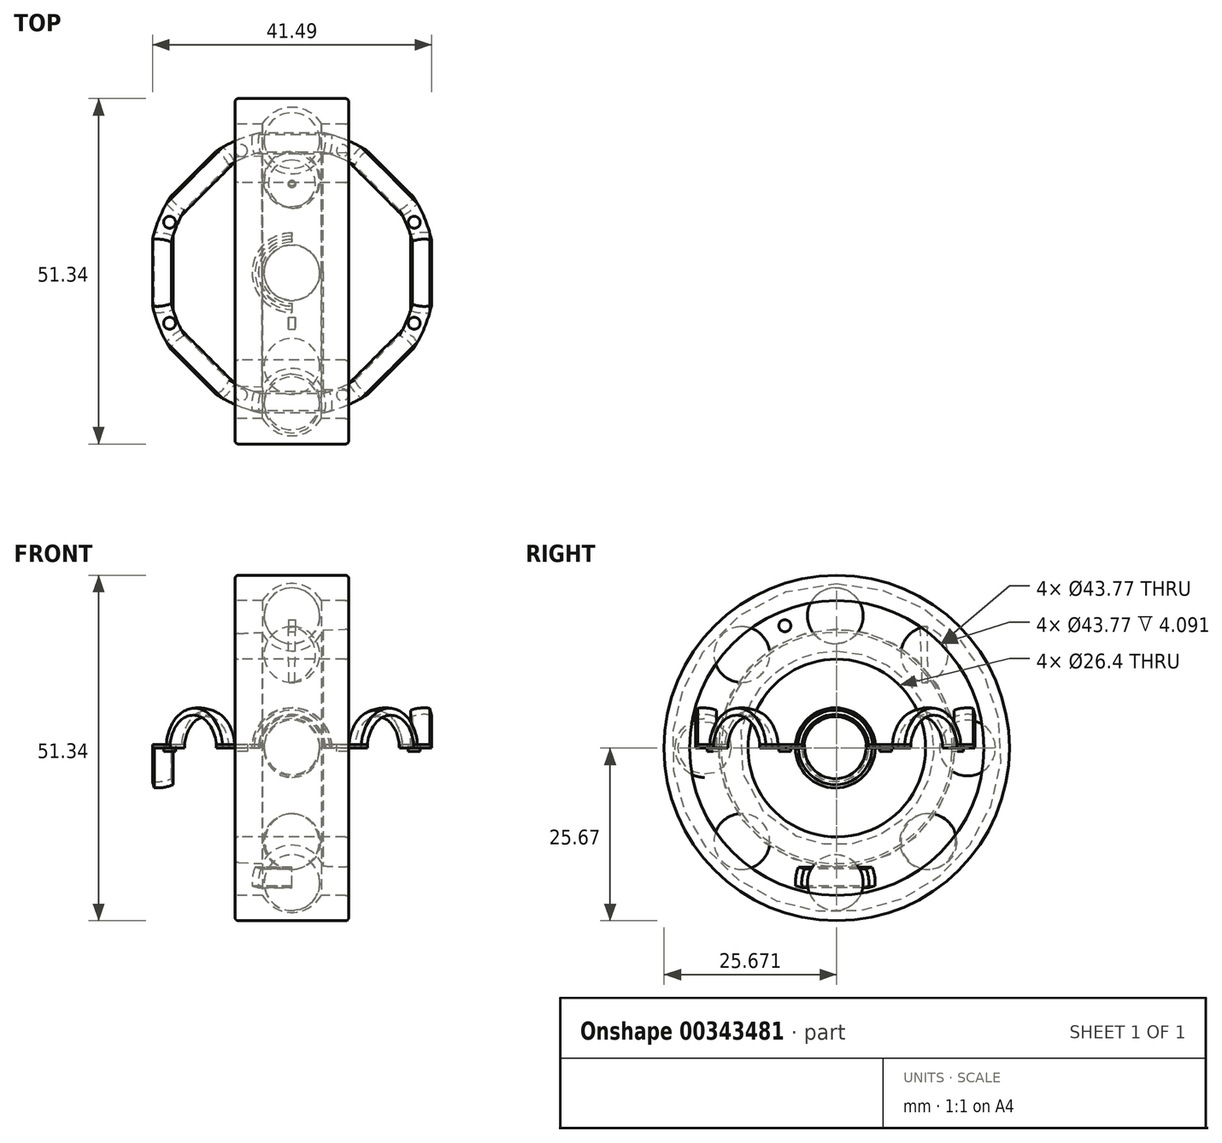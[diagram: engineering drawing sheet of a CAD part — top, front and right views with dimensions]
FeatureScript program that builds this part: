
annotation { "Feature Type Name" : "Feature", "Feature Type Description" : "" }
export const myFeature = defineFeature(function(context is Context, id is Id, definition is map)
    precondition{}
    {
        {
            assignVariable(context, id + "F0", {"name" : "t", "anyValue" : .5});
        }
        {
            var Q0;
            Q0=qCreatedBy(makeId("Top.planeOp"),FACE);
            var sketch = newSketch(context, id + "F1", { "sketchPlane" : qUnion([Q0])});
            skArc(sketch, "E0", {"start": v(-10.48, 32.8) * mm, "mid": v(-10.5, 31.35) * mm, "end": v(-10.18, 29.94) * mm});
            skArc(sketch, "E1", {"start": v(0.12, 30.21) * mm, "mid": v(-4.57, 36.97) * mm, "end": v(-9.25, 30.21) * mm});
            skCircle(sketch, "E2", {"center": v(-4.57, 31.97) * mm, "radius": 4.14 * mm});
            skCircle(sketch, "E3", {"center": v(-4.57, 12.32) * mm, "radius": 18.5 * mm});
            skCircle(sketch, "E4", {"center": v(-4.57, 12.32) * mm, "radius": 21.32 * mm});
            skArc(sketch, "E5", {"start": v(5.74, 30.98) * mm, "mid": v(4.7, 29.98) * mm, "end": v(3.93, 28.75) * mm});
            skArc(sketch, "E6", {"start": v(11.4, 21.66) * mm, "mid": v(12.86, 29.75) * mm, "end": v(4.78, 28.28) * mm});
            skCircle(sketch, "E7", {"center": v(9.33, 26.21) * mm, "radius": 4.14 * mm});
            skArc(sketch, "E8", {"start": v(15.91, 18.23) * mm, "mid": v(14.47, 18.26) * mm, "end": v(13.06, 17.93) * mm});
            skArc(sketch, "E9", {"start": v(13.33, 7.63) * mm, "mid": v(20.08, 12.32) * mm, "end": v(13.33, 17) * mm});
            skCircle(sketch, "E10", {"center": v(15.08, 12.32) * mm, "radius": 4.14 * mm});
            skArc(sketch, "E11", {"start": v(14.1, 2.02) * mm, "mid": v(13.1, 3.06) * mm, "end": v(11.87, 3.82) * mm});
            skArc(sketch, "E12", {"start": v(4.78, -3.65) * mm, "mid": v(12.86, -5.11) * mm, "end": v(11.4, 2.97) * mm});
            skCircle(sketch, "E13", {"center": v(9.33, -1.58) * mm, "radius": 4.14 * mm});
            skArc(sketch, "E14", {"start": v(1.35, -8.16) * mm, "mid": v(1.37, -6.72) * mm, "end": v(1.05, -5.31) * mm});
            skArc(sketch, "E15", {"start": v(-9.25, -5.58) * mm, "mid": v(-4.57, -12.33) * mm, "end": v(0.12, -5.58) * mm});
            skCircle(sketch, "E16", {"center": v(-4.57, -7.33) * mm, "radius": 4.14 * mm});
            skArc(sketch, "E17", {"start": v(-14.87, -6.35) * mm, "mid": v(-13.83, -5.34) * mm, "end": v(-13.06, -4.12) * mm});
            skArc(sketch, "E18", {"start": v(-20.53, 2.97) * mm, "mid": v(-22, -5.11) * mm, "end": v(-13.9, -3.65) * mm});
            skCircle(sketch, "E19", {"center": v(-18.46, -1.58) * mm, "radius": 4.14 * mm});
            skArc(sketch, "E20", {"start": v(-25.05, 6.4) * mm, "mid": v(-23.62, 6.47) * mm, "end": v(-22.25, 6.87) * mm});
            skArc(sketch, "E21", {"start": v(-22.5, 16.87) * mm, "mid": v(-29.57, 12.32) * mm, "end": v(-22.5, 7.77) * mm});
            skCircle(sketch, "E22", {"center": v(-24.57, 12.32) * mm, "radius": 4.14 * mm});
            skArc(sketch, "E23", {"start": v(-23.23, 22.62) * mm, "mid": v(-22.23, 21.58) * mm, "end": v(-21, 20.8) * mm});
            skArc(sketch, "E24", {"start": v(-13.9, 28.28) * mm, "mid": v(-22, 29.75) * mm, "end": v(-20.53, 21.66) * mm});
            skCircle(sketch, "E25", {"center": v(-18.46, 26.21) * mm, "radius": 4.14 * mm});
            skArc(sketch, "E26", {"start": v(-14.5, 29.26) * mm, "mid": v(-12.08, 30.46) * mm, "end": v(-9.52, 31.32) * mm});
            skArc(sketch, "E27", {"start": v(0.4, 31.32) * mm, "mid": v(2.95, 30.46) * mm, "end": v(5.37, 29.26) * mm});
            skArc(sketch, "E28", {"start": v(12.38, 22.25) * mm, "mid": v(13.58, 19.83) * mm, "end": v(14.44, 17.27) * mm});
            skArc(sketch, "E29", {"start": v(14.44, 7.36) * mm, "mid": v(13.58, 4.8) * mm, "end": v(12.38, 2.38) * mm});
            skArc(sketch, "E30", {"start": v(5.37, -4.63) * mm, "mid": v(2.95, -5.83) * mm, "end": v(0.4, -6.7) * mm});
            skArc(sketch, "E31", {"start": v(-9.52, -6.7) * mm, "mid": v(-12.08, -5.83) * mm, "end": v(-14.5, -4.63) * mm});
            skArc(sketch, "E32", {"start": v(-21.53, 2.37) * mm, "mid": v(-22.75, 4.82) * mm, "end": v(-23.61, 7.41) * mm});
            skArc(sketch, "E33", {"start": v(-23.6, 17.22) * mm, "mid": v(-22.74, 19.82) * mm, "end": v(-21.53, 22.26) * mm});
            skCircle(sketch, "E34", {"center": v(-12.08, 30.46) * mm, "radius": 0.89 * mm});
            skCircle(sketch, "E35", {"center": v(2.95, 30.46) * mm, "radius": 0.89 * mm});
            skCircle(sketch, "E36", {"center": v(13.58, 19.83) * mm, "radius": 0.89 * mm});
            skCircle(sketch, "E37", {"center": v(13.6, 4.82) * mm, "radius": 0.89 * mm});
            skCircle(sketch, "E38", {"center": v(13.62, 19.81) * mm, "radius": 0.89 * mm});
            skCircle(sketch, "E39", {"center": v(-22.74, 19.82) * mm, "radius": 0.89 * mm});
            skCircle(sketch, "E40", {"center": v(-22.75, 4.82) * mm, "radius": 0.89 * mm});
            skCircle(sketch, "E41", {"center": v(-12.08, -5.83) * mm, "radius": 0.89 * mm});
            skCircle(sketch, "E42", {"center": v(2.95, -5.83) * mm, "radius": 0.89 * mm});
            skSolve(sketch);
        }
        {
            var Q0;
            Q0=qCreatedBy(makeId("Top.planeOp"),FACE);
            var sketch = newSketch(context, id + "F2", { "sketchPlane" : qUnion([Q0])});
            skLineSegment(sketch, "E43.0", {"start": v(-14.32, 26.05) * mm, "end": v(-14.32, 26.05) * mm});
            skLineSegment(sketch, "E43.1", {"start": v(-20.43, 12.32) * mm, "end": v(-20.43, 12.32) * mm});
            skArc(sketch, "E43.2", {"start": v(-0.42, 31.97) * mm, "mid": v(-4.57, 36.1) * mm, "end": v(-8.7, 31.97) * mm});
            skLineSegment(sketch, "E43.3", {"start": v(5.19, 26.08) * mm, "end": v(5.19, 26.08) * mm});
            skLineSegment(sketch, "E43.4", {"start": v(10.94, 12.32) * mm, "end": v(10.94, 12.32) * mm});
            skLineSegment(sketch, "E43.5", {"start": v(5.19, -1.58) * mm, "end": v(5.19, -1.58) * mm});
            skArc(sketch, "E43.6", {"start": v(-0.43, -7.08) * mm, "mid": v(-4.6, -3.2) * mm, "end": v(-8.7, -7.14) * mm});
            skLineSegment(sketch, "E43.7", {"start": v(-14.32, -1.58) * mm, "end": v(-14.32, -1.58) * mm});
            skPoint(sketch, "E43.8", {"position": v(-4.57, 31.97) * mm});
            skPoint(sketch, "E43.9", {"position": v(-18.46, 26.21) * mm});
            skPoint(sketch, "E43.10", {"position": v(-24.57, 12.32) * mm});
            skPoint(sketch, "E43.11", {"position": v(-18.46, -1.58) * mm});
            skPoint(sketch, "E43.12", {"position": v(-4.57, -7.33) * mm});
            skPoint(sketch, "E43.13", {"position": v(9.33, -1.58) * mm});
            skPoint(sketch, "E43.14", {"position": v(15.08, 12.32) * mm});
            skPoint(sketch, "E43.15", {"position": v(9.33, 26.21) * mm});
            skLineSegment(sketch, "E44", {"start": v(-42.22, 31.97) * mm, "end": v(40.03, 31.97) * mm});
            skArc(sketch, "E45.0", {"start": v(-14.32, 26.05) * mm, "mid": v(-18.38, 30.35) * mm, "end": v(-22.6, 26.21) * mm});
            skArc(sketch, "E45.1", {"start": v(13.47, 26.03) * mm, "mid": v(9.36, 30.35) * mm, "end": v(5.19, 26.08) * mm});
            skArc(sketch, "E45.2", {"start": v(19.23, 12.32) * mm, "mid": v(15.08, 16.46) * mm, "end": v(10.94, 12.32) * mm});
            skArc(sketch, "E45.3", {"start": v(13.47, -1.58) * mm, "mid": v(9.33, 2.56) * mm, "end": v(5.19, -1.58) * mm});
            skArc(sketch, "E45.4", {"start": v(-14.32, -1.58) * mm, "mid": v(-18.46, 2.56) * mm, "end": v(-22.6, -1.58) * mm});
            skArc(sketch, "E45.5", {"start": v(-20.43, 12.32) * mm, "mid": v(-24.57, 16.46) * mm, "end": v(-28.72, 12.32) * mm});
            skLineSegment(sketch, "E46", {"start": v(-22.6, 26.21) * mm, "end": v(-14.32, 26.05) * mm});
            skLineSegment(sketch, "E47", {"start": v(5.19, 26.08) * mm, "end": v(13.47, 26.03) * mm});
            skLineSegment(sketch, "E48", {"start": v(-28.72, 12.32) * mm, "end": v(19.23, 12.32) * mm});
            skLineSegment(sketch, "E49", {"start": v(-8.7, -7.14) * mm, "end": v(-0.43, -7.08) * mm});
            skLineSegment(sketch, "E50", {"start": v(-18.46, -1.58) * mm, "end": v(9.33, -1.58) * mm});
            skLineSegment(sketch, "E51", {"start": v(9.33, -1.58) * mm, "end": v(16.13, -1.58) * mm});
            skLineSegment(sketch, "E52", {"start": v(-18.46, -1.58) * mm, "end": v(-25.22, -1.58) * mm});
            skSolve(sketch);
        }
        {
            var Q0;
            {var subQ0=sQuery(id+"F2.wireOp",EDGE,"E46");Q0=makeQuery(id+"F2.imprint","IMPRINT",FACE,{"disambiguationData":[TD([[makeQuery(id+"F2.imprint","IMPRINT",EDGE,{"derivedFrom":subQ0}),1.0]])]});}
            var Q1;
            {var subQ0=sQuery(id+"F2.wireOp",EDGE,"E47");Q1=makeQuery(id+"F2.imprint","IMPRINT",FACE,{"disambiguationData":[TD([[makeQuery(id+"F2.imprint","IMPRINT",EDGE,{"derivedFrom":subQ0}),1.0]])]});}
            var Q2;
            Q2=sQuery(id+"F2.wireOp",EDGE,"E46");
            revolve(context, id + "F3", {"entities" : qUnion([Q0, Q1]), "axis" : qUnion([Q2]), "revolveType" : RevolveType.FULL});
        }
        {
            var Q0;
            {var subQ0=sQuery(id+"F2.wireOp",EDGE,"E43.2");Q0=makeQuery(id+"F2.imprint","IMPRINT",FACE,{"disambiguationData":[TD([[makeQuery(id+"F2.imprint","IMPRINT",EDGE,{"derivedFrom":subQ0}),1.0]])]});}
            var Q1;
            Q1=sQuery(id+"F2.wireOp",EDGE,"E44");
            revolve(context, id + "F4", {"entities" : qUnion([Q0]), "axis" : qUnion([Q1]), "revolveType" : RevolveType.FULL});
        }
        {
            var Q0;
            {var subQ0=sQuery(id+"F2.wireOp",EDGE,"E45.5");Q0=makeQuery(id+"F2.imprint","IMPRINT",FACE,{"disambiguationData":[TD([[makeQuery(id+"F2.imprint","IMPRINT",EDGE,{"derivedFrom":subQ0}),1.0]])]});}
            var Q1;
            {var subQ0=sQuery(id+"F2.wireOp",EDGE,"E45.2");Q1=makeQuery(id+"F2.imprint","IMPRINT",FACE,{"disambiguationData":[TD([[makeQuery(id+"F2.imprint","IMPRINT",EDGE,{"derivedFrom":subQ0}),1.0]])]});}
            var Q2;
            Q2=sQuery(id+"F2.wireOp",EDGE,"E48");
            revolve(context, id + "F5", {"entities" : qUnion([Q0, Q1]), "axis" : qUnion([Q2]), "revolveType" : RevolveType.FULL});
        }
        {
            var Q0;
            {var subQ0=sQuery(id+"F2.wireOp",EDGE,"E45.3");Q0=makeQuery(id+"F2.imprint","IMPRINT",FACE,{"disambiguationData":[TD([[makeQuery(id+"F2.imprint","IMPRINT",EDGE,{"derivedFrom":subQ0}),1.0]])]});}
            var Q1;
            {var subQ0=sQuery(id+"F2.wireOp",EDGE,"E45.4");Q1=makeQuery(id+"F2.imprint","IMPRINT",FACE,{"disambiguationData":[TD([[makeQuery(id+"F2.imprint","IMPRINT",EDGE,{"derivedFrom":subQ0}),1.0]])]});}
            var Q2;
            Q2=sQuery(id+"F2.wireOp",EDGE,"E50");
            revolve(context, id + "F6", {"entities" : qUnion([Q0, Q1]), "axis" : qUnion([Q2]), "revolveType" : RevolveType.FULL});
        }
        {
            var Q0;
            Q0=makeQuery(id+"F2.imprint","IMPRINT",FACE,{"disambiguationData":[TD([[makeQuery(id+"F2.imprint","IMPRINT",EDGE,{"derivedFrom":sQuery(id+"F2.wireOp",EDGE,"E43.6")}),1.0]])]});
            var Q1;
            Q1=sQuery(id+"F2.wireOp",EDGE,"E49");
            revolve(context, id + "F7", {"entities" : qUnion([Q0]), "axis" : qUnion([Q1]), "revolveType" : RevolveType.FULL});
        }
        {
            var Q0;
            Q0=qCreatedBy(makeId("Top.planeOp"),FACE);
            var sketch = newSketch(context, id + "F8", { "sketchPlane" : qUnion([Q0])});
            skArc(sketch, "E53.0", {"start": v(-23.23, 22.62) * mm, "mid": v(-22.23, 21.58) * mm, "end": v(-21, 20.8) * mm});
            skArc(sketch, "E53.1", {"start": v(-25.05, 6.4) * mm, "mid": v(-23.62, 6.47) * mm, "end": v(-22.25, 6.87) * mm});
            skArc(sketch, "E53.2", {"start": v(-10.48, 32.8) * mm, "mid": v(-10.5, 31.35) * mm, "end": v(-10.18, 29.94) * mm});
            skArc(sketch, "E53.3", {"start": v(5.74, 30.98) * mm, "mid": v(4.7, 29.98) * mm, "end": v(3.93, 28.75) * mm});
            skArc(sketch, "E53.4", {"start": v(15.91, 18.23) * mm, "mid": v(14.47, 18.26) * mm, "end": v(13.06, 17.93) * mm});
            skArc(sketch, "E53.5", {"start": v(14.1, 2.02) * mm, "mid": v(13.1, 3.06) * mm, "end": v(11.87, 3.82) * mm});
            skArc(sketch, "E53.6", {"start": v(1.35, -8.16) * mm, "mid": v(1.37, -6.72) * mm, "end": v(1.05, -5.31) * mm});
            skArc(sketch, "E53.7", {"start": v(-14.87, -6.35) * mm, "mid": v(-13.83, -5.34) * mm, "end": v(-13.06, -4.12) * mm});
            skPoint(sketch, "E53.8", {"position": v(-4.57, 31.97) * mm});
            skPoint(sketch, "E53.9", {"position": v(9.33, 26.21) * mm});
            skPoint(sketch, "E53.10", {"position": v(15.08, 12.32) * mm});
            skPoint(sketch, "E53.11", {"position": v(9.33, -1.58) * mm});
            skPoint(sketch, "E53.12", {"position": v(-4.57, -7.33) * mm});
            skPoint(sketch, "E53.13", {"position": v(-18.46, -1.58) * mm});
            skPoint(sketch, "E53.14", {"position": v(-24.57, 12.32) * mm});
            skPoint(sketch, "E53.15", {"position": v(-18.46, 26.21) * mm});
            skArc(sketch, "E53.16", {"start": v(0.12, 30.21) * mm, "mid": v(0.42, 31.63) * mm, "end": v(0.31, 33.07) * mm});
            skArc(sketch, "E53.17", {"start": v(11.4, 21.66) * mm, "mid": v(12.62, 22.44) * mm, "end": v(13.56, 23.54) * mm});
            skArc(sketch, "E53.18", {"start": v(13.33, 7.63) * mm, "mid": v(14.74, 7.33) * mm, "end": v(16.19, 7.44) * mm});
            skArc(sketch, "E53.19", {"start": v(4.78, -3.65) * mm, "mid": v(5.56, -4.87) * mm, "end": v(6.66, -5.8) * mm});
            skArc(sketch, "E53.20", {"start": v(-9.25, -5.58) * mm, "mid": v(-9.55, -7) * mm, "end": v(-9.44, -8.44) * mm});
            skArc(sketch, "E53.21", {"start": v(-20.53, 2.97) * mm, "mid": v(-21.75, 2.19) * mm, "end": v(-22.69, 1.1) * mm});
            skArc(sketch, "E53.22", {"start": v(-22.5, 16.87) * mm, "mid": v(-23.87, 17.27) * mm, "end": v(-25.3, 17.27) * mm});
            skArc(sketch, "E53.23", {"start": v(-13.9, 28.28) * mm, "mid": v(-14.7, 29.5) * mm, "end": v(-15.8, 30.44) * mm});
            skCircle(sketch, "E54.0", {"center": v(-4.57, 12.32) * mm, "radius": 21.32 * mm});
            skCircle(sketch, "E55.0", {"center": v(-4.57, 12.32) * mm, "radius": 18.5 * mm});
            skArc(sketch, "E56.trimOffspring", {"start": v(-22.69, 23.54) * mm, "mid": v(-21.75, 22.44) * mm, "end": v(-20.53, 21.66) * mm});
            skArc(sketch, "E57.trimOffspring", {"start": v(-9.44, 33.07) * mm, "mid": v(-9.55, 31.63) * mm, "end": v(-9.25, 30.21) * mm});
            skArc(sketch, "E58.trimOffspring", {"start": v(6.66, 30.44) * mm, "mid": v(5.56, 29.5) * mm, "end": v(4.78, 28.28) * mm});
            skArc(sketch, "E59.trimOffspring", {"start": v(16.19, 17.2) * mm, "mid": v(14.74, 17.3) * mm, "end": v(13.33, 17) * mm});
            skArc(sketch, "E60.trimOffspring", {"start": v(13.56, 1.1) * mm, "mid": v(12.62, 2.19) * mm, "end": v(11.4, 2.97) * mm});
            skArc(sketch, "E61.trimOffspring", {"start": v(0.31, -8.44) * mm, "mid": v(0.42, -7) * mm, "end": v(0.12, -5.58) * mm});
            skArc(sketch, "E62.trimOffspring", {"start": v(-15.8, -5.8) * mm, "mid": v(-14.7, -4.87) * mm, "end": v(-13.9, -3.65) * mm});
            skArc(sketch, "E63.trimOffspring", {"start": v(-25.3, 7.37) * mm, "mid": v(-23.87, 7.37) * mm, "end": v(-22.5, 7.77) * mm});
            skLineSegment(sketch, "E64", {"start": v(-18.46, -1.58) * mm, "end": v(9.33, 26.21) * mm, "construction": true});
            skLineSegment(sketch, "E65", {"start": v(-18.46, 26.21) * mm, "end": v(9.33, -1.58) * mm, "construction": true});
            skLineSegment(sketch, "E66", {"start": v(-24.57, 12.32) * mm, "end": v(15.08, 12.32) * mm, "construction": true});
            skLineSegment(sketch, "E67", {"start": v(-4.57, 31.97) * mm, "end": v(-4.57, -7.33) * mm, "construction": true});
            skSolve(sketch);
        }
        {
            var Q0;
            {var subQ0=sQuery(id+"F8.wireOp",EDGE,"E53.0");Q0=makeQuery(id+"F8.imprint","IMPRINT",FACE,{"disambiguationData":[TD([[makeQuery(id+"F8.imprint","IMPRINT",EDGE,{"derivedFrom":subQ0}),1.0]])]});}
            var Q1;
            Q1=sQuery(id+"F8.wireOp",EDGE,"E65");
            revolve(context, id + "F9", {"entities" : qUnion([Q0]), "axis" : qUnion([Q1]), "revolveType" : RevolveType.ONE_DIRECTION, "oppositeDirection" : true, "angle" : 180 * degree});
        }
        {
            var Q0;
            {var subQ0=sQuery(id+"F8.wireOp",EDGE,"E53.2");Q0=makeQuery(id+"F8.imprint","IMPRINT",FACE,{"disambiguationData":[TD([[makeQuery(id+"F8.imprint","IMPRINT",EDGE,{"derivedFrom":subQ0}),1.0]])]});}
            var Q1;
            Q1=sQuery(id+"F8.wireOp",EDGE,"E67");
            revolve(context, id + "F10", {"entities" : qUnion([Q0]), "axis" : qUnion([Q1]), "revolveType" : RevolveType.ONE_DIRECTION, "oppositeDirection" : true, "angle" : 180 * degree});
        }
        {
            var Q0;
            {var subQ0=sQuery(id+"F8.wireOp",EDGE,"E53.3");Q0=makeQuery(id+"F8.imprint","IMPRINT",FACE,{"disambiguationData":[TD([[makeQuery(id+"F8.imprint","IMPRINT",EDGE,{"derivedFrom":subQ0}),1.0]])]});}
            var Q1;
            Q1=sQuery(id+"F8.wireOp",EDGE,"E64");
            revolve(context, id + "F11", {"entities" : qUnion([Q0]), "axis" : qUnion([Q1]), "revolveType" : RevolveType.ONE_DIRECTION, "angle" : 180 * degree});
        }
        {
            var Q0;
            {var subQ0=sQuery(id+"F8.wireOp",EDGE,"E53.4");Q0=makeQuery(id+"F8.imprint","IMPRINT",FACE,{"disambiguationData":[TD([[makeQuery(id+"F8.imprint","IMPRINT",EDGE,{"derivedFrom":subQ0}),1.0]])]});}
            var Q1;
            Q1=sQuery(id+"F8.wireOp",EDGE,"E66");
            revolve(context, id + "F12", {"entities" : qUnion([Q0]), "axis" : qUnion([Q1]), "revolveType" : RevolveType.ONE_DIRECTION, "angle" : 180 * degree});
        }
        {
            var Q0;
            {var subQ0=sQuery(id+"F8.wireOp",EDGE,"E53.5");Q0=makeQuery(id+"F8.imprint","IMPRINT",FACE,{"disambiguationData":[TD([[makeQuery(id+"F8.imprint","IMPRINT",EDGE,{"derivedFrom":subQ0}),1.0]])]});}
            var Q1;
            Q1=sQuery(id+"F8.wireOp",EDGE,"E65");
            revolve(context, id + "F13", {"entities" : qUnion([Q0]), "axis" : qUnion([Q1]), "revolveType" : RevolveType.ONE_DIRECTION, "angle" : 180 * degree});
        }
        {
            var Q0;
            {var subQ0=sQuery(id+"F8.wireOp",EDGE,"E53.6");Q0=makeQuery(id+"F8.imprint","IMPRINT",FACE,{"disambiguationData":[TD([[makeQuery(id+"F8.imprint","IMPRINT",EDGE,{"derivedFrom":subQ0}),1.0]])]});}
            var Q1;
            Q1=sQuery(id+"F8.wireOp",EDGE,"E67");
            revolve(context, id + "F14", {"entities" : qUnion([Q0]), "axis" : qUnion([Q1]), "revolveType" : RevolveType.ONE_DIRECTION, "angle" : 180 * degree});
        }
        {
            var Q0;
            {var subQ0=sQuery(id+"F8.wireOp",EDGE,"E53.7");Q0=makeQuery(id+"F8.imprint","IMPRINT",FACE,{"disambiguationData":[TD([[makeQuery(id+"F8.imprint","IMPRINT",EDGE,{"derivedFrom":subQ0}),1.0]])]});}
            var Q1;
            Q1=sQuery(id+"F8.wireOp",EDGE,"E64");
            revolve(context, id + "F15", {"entities" : qUnion([Q0]), "axis" : qUnion([Q1]), "revolveType" : RevolveType.ONE_DIRECTION, "oppositeDirection" : true, "angle" : 180 * degree});
        }
        {
            var Q0;
            {var subQ0=sQuery(id+"F8.wireOp",EDGE,"E53.1");Q0=makeQuery(id+"F8.imprint","IMPRINT",FACE,{"disambiguationData":[TD([[makeQuery(id+"F8.imprint","IMPRINT",EDGE,{"derivedFrom":subQ0}),1.0]])]});}
            var Q1;
            Q1=sQuery(id+"F8.wireOp",EDGE,"E66");
            revolve(context, id + "F16", {"entities" : qUnion([Q0]), "axis" : qUnion([Q1]), "revolveType" : RevolveType.ONE_DIRECTION, "oppositeDirection" : true, "angle" : 180 * degree});
        }
        {
            var Q0;
            Q0=qCreatedBy(makeId("Top.planeOp"),FACE);
            var sketch = newSketch(context, id + "F17", { "sketchPlane" : qUnion([Q0])});
            skArc(sketch, "E68.0", {"start": v(-13.9, 28.28) * mm, "mid": v(-14.7, 29.5) * mm, "end": v(-15.8, 30.44) * mm});
            skArc(sketch, "E68.1", {"start": v(-9.44, 33.07) * mm, "mid": v(-9.55, 31.63) * mm, "end": v(-9.25, 30.21) * mm});
            skArc(sketch, "E68.2", {"start": v(0.12, 30.21) * mm, "mid": v(0.42, 31.63) * mm, "end": v(0.31, 33.07) * mm});
            skArc(sketch, "E68.3", {"start": v(6.66, 30.44) * mm, "mid": v(5.56, 29.5) * mm, "end": v(4.78, 28.28) * mm});
            skArc(sketch, "E68.4", {"start": v(11.4, 21.66) * mm, "mid": v(12.62, 22.44) * mm, "end": v(13.56, 23.54) * mm});
            skArc(sketch, "E68.5", {"start": v(16.19, 17.2) * mm, "mid": v(14.74, 17.3) * mm, "end": v(13.33, 17) * mm});
            skArc(sketch, "E68.6", {"start": v(13.33, 7.63) * mm, "mid": v(14.74, 7.33) * mm, "end": v(16.19, 7.44) * mm});
            skArc(sketch, "E68.7", {"start": v(13.56, 1.1) * mm, "mid": v(12.62, 2.19) * mm, "end": v(11.4, 2.97) * mm});
            skArc(sketch, "E68.8", {"start": v(4.78, -3.65) * mm, "mid": v(5.56, -4.87) * mm, "end": v(6.66, -5.8) * mm});
            skArc(sketch, "E68.10", {"start": v(-9.25, -5.58) * mm, "mid": v(-9.55, -7) * mm, "end": v(-9.44, -8.44) * mm});
            skArc(sketch, "E68.11", {"start": v(-15.8, -5.8) * mm, "mid": v(-14.7, -4.87) * mm, "end": v(-13.9, -3.65) * mm});
            skArc(sketch, "E68.12", {"start": v(-20.53, 2.97) * mm, "mid": v(-21.75, 2.19) * mm, "end": v(-22.69, 1.1) * mm});
            skArc(sketch, "E68.13", {"start": v(-25.3, 7.37) * mm, "mid": v(-23.87, 7.37) * mm, "end": v(-22.5, 7.77) * mm});
            skArc(sketch, "E68.14", {"start": v(-22.5, 16.87) * mm, "mid": v(-23.87, 17.27) * mm, "end": v(-25.3, 17.27) * mm});
            skArc(sketch, "E68.15", {"start": v(-22.69, 23.54) * mm, "mid": v(-21.75, 22.44) * mm, "end": v(-20.53, 21.66) * mm});
            skCircle(sketch, "E68.16", {"center": v(-4.57, 12.32) * mm, "radius": 18.5 * mm});
            skCircle(sketch, "E68.17", {"center": v(-4.57, 12.32) * mm, "radius": 21.32 * mm});
            skCircle(sketch, "E69.0", {"center": v(-12.08, 30.46) * mm, "radius": 0.89 * mm});
            skCircle(sketch, "E69.1", {"center": v(-22.74, 19.82) * mm, "radius": 0.89 * mm});
            skCircle(sketch, "E69.2", {"center": v(2.95, 30.46) * mm, "radius": 0.89 * mm});
            skCircle(sketch, "E69.3", {"center": v(13.62, 19.81) * mm, "radius": 0.89 * mm});
            skCircle(sketch, "E69.4", {"center": v(13.6, 4.82) * mm, "radius": 0.89 * mm});
            skCircle(sketch, "E69.5", {"center": v(2.95, -5.83) * mm, "radius": 0.89 * mm});
            skCircle(sketch, "E69.6", {"center": v(-12.08, -5.83) * mm, "radius": 0.89 * mm});
            skCircle(sketch, "E69.7", {"center": v(-22.75, 4.82) * mm, "radius": 0.89 * mm});
            skArc(sketch, "E70.0", {"start": v(0.31, -8.44) * mm, "mid": v(0.42, -7) * mm, "end": v(0.12, -5.58) * mm});
            skSolve(sketch);
        }
        {
            var Q0;
            {var subQ1=sQuery(id+"F17.wireOp",EDGE,"E68.6");Q0=makeQuery(id+"F17.imprint","IMPRINT",FACE,{"disambiguationData":[TD([[makeQuery(id+"F17.imprint","IMPRINT",EDGE,{"derivedFrom":subQ1}),-1.0]])]});}
            var Q1;
            {var subQ1=sQuery(id+"F17.wireOp",EDGE,"E68.8");Q1=makeQuery(id+"F17.imprint","IMPRINT",FACE,{"disambiguationData":[TD([[makeQuery(id+"F17.imprint","IMPRINT",EDGE,{"derivedFrom":subQ1}),-1.0]])]});}
            var Q2;
            {var subQ1=sQuery(id+"F17.wireOp",EDGE,"E68.10");Q2=makeQuery(id+"F17.imprint","IMPRINT",FACE,{"disambiguationData":[TD([[makeQuery(id+"F17.imprint","IMPRINT",EDGE,{"derivedFrom":subQ1}),-1.0]])]});}
            var Q3;
            {var subQ1=sQuery(id+"F17.wireOp",EDGE,"E68.12");Q3=makeQuery(id+"F17.imprint","IMPRINT",FACE,{"disambiguationData":[TD([[makeQuery(id+"F17.imprint","IMPRINT",EDGE,{"derivedFrom":subQ1}),-1.0]])]});}
            var Q4;
            {var subQ1=sQuery(id+"F17.wireOp",EDGE,"E68.14");Q4=makeQuery(id+"F17.imprint","IMPRINT",FACE,{"disambiguationData":[TD([[makeQuery(id+"F17.imprint","IMPRINT",EDGE,{"derivedFrom":subQ1}),-1.0]])]});}
            var Q5;
            {var subQ1=sQuery(id+"F17.wireOp",EDGE,"E68.0");Q5=makeQuery(id+"F17.imprint","IMPRINT",FACE,{"disambiguationData":[TD([[makeQuery(id+"F17.imprint","IMPRINT",EDGE,{"derivedFrom":subQ1}),-1.0]])]});}
            var Q6;
            {var subQ1=sQuery(id+"F17.wireOp",EDGE,"E68.2");Q6=makeQuery(id+"F17.imprint","IMPRINT",FACE,{"disambiguationData":[TD([[makeQuery(id+"F17.imprint","IMPRINT",EDGE,{"derivedFrom":subQ1}),-1.0]])]});}
            var Q7;
            {var subQ1=sQuery(id+"F17.wireOp",EDGE,"E68.4");Q7=makeQuery(id+"F17.imprint","IMPRINT",FACE,{"disambiguationData":[TD([[makeQuery(id+"F17.imprint","IMPRINT",EDGE,{"derivedFrom":subQ1}),-1.0]])]});}
            extrude(context, id + "F18", {"entities" : qUnion([Q0, Q1, Q2, Q3, Q4, Q5, Q6, Q7]), "depth" : (getVariable(context, 't')) * mm});
        }
        {
            var Q0;
            Q0=makeQuery(id+"F16.opRevolve","SWEPT_BODY",BODY,{"disambiguationData":[OSD([sQuery(id+"F8.wireOp",EDGE,"E53.1"),sQuery(id+"F8.wireOp",EDGE,"E54.0"),sQuery(id+"F8.wireOp",EDGE,"E55.0"),sQuery(id+"F8.wireOp",EDGE,"E63.trimOffspring")])]});
            transform(context, id + "F19", {"entities" : qUnion([Q0]), "transformType" : TransformType.COPY});
        }
        {
            var Q0;
            Q0=makeQuery(id+"F19.opPattern","COPY",BODY,{"derivedFrom":makeQuery(id+"F16.opRevolve","SWEPT_BODY",BODY,{"disambiguationData":[OSD([sQuery(id+"F8.wireOp",EDGE,"E53.1"),sQuery(id+"F8.wireOp",EDGE,"E54.0"),sQuery(id+"F8.wireOp",EDGE,"E55.0"),sQuery(id+"F8.wireOp",EDGE,"E63.trimOffspring")])]}),"instanceName":"1"});
            var Q1;
            Q1=sQuery(id+"F2.wireOp",EDGE,"E48");
            transform(context, id + "F20", {"entities" : qUnion([Q0]), "transformType" : TransformType.ROTATION, "transformAxis" : qUnion([Q1]), "angle" : 180 * degree, "makeCopy" : false});
        }
        {
            var Q0;
            Q0=makeQuery(id+"F17.imprint","IMPRINT",FACE,{"disambiguationData":[TD([[makeQuery(id+"F17.imprint","IMPRINT",EDGE,{"derivedFrom":sQuery(id+"F17.wireOp",EDGE,"E69.6")}),1.0]])]});
            var Q1;
            Q1=makeQuery(id+"F17.imprint","IMPRINT",FACE,{"disambiguationData":[TD([[makeQuery(id+"F17.imprint","IMPRINT",EDGE,{"derivedFrom":sQuery(id+"F17.wireOp",EDGE,"E69.7")}),1.0]])]});
            var Q2;
            Q2=makeQuery(id+"F17.imprint","IMPRINT",FACE,{"disambiguationData":[TD([[makeQuery(id+"F17.imprint","IMPRINT",EDGE,{"derivedFrom":sQuery(id+"F17.wireOp",EDGE,"E69.1")}),1.0]])]});
            var Q3;
            Q3=makeQuery(id+"F17.imprint","IMPRINT",FACE,{"disambiguationData":[TD([[makeQuery(id+"F17.imprint","IMPRINT",EDGE,{"derivedFrom":sQuery(id+"F17.wireOp",EDGE,"E69.0")}),1.0]])]});
            var Q4;
            Q4=makeQuery(id+"F17.imprint","IMPRINT",FACE,{"disambiguationData":[TD([[makeQuery(id+"F17.imprint","IMPRINT",EDGE,{"derivedFrom":sQuery(id+"F17.wireOp",EDGE,"E69.2")}),1.0]])]});
            var Q5;
            Q5=makeQuery(id+"F17.imprint","IMPRINT",FACE,{"disambiguationData":[TD([[makeQuery(id+"F17.imprint","IMPRINT",EDGE,{"derivedFrom":sQuery(id+"F17.wireOp",EDGE,"E69.3")}),1.0]])]});
            var Q6;
            Q6=makeQuery(id+"F17.imprint","IMPRINT",FACE,{"disambiguationData":[TD([[makeQuery(id+"F17.imprint","IMPRINT",EDGE,{"derivedFrom":sQuery(id+"F17.wireOp",EDGE,"E69.4")}),1.0]])]});
            var Q7;
            Q7=makeQuery(id+"F17.imprint","IMPRINT",FACE,{"disambiguationData":[TD([[makeQuery(id+"F17.imprint","IMPRINT",EDGE,{"derivedFrom":sQuery(id+"F17.wireOp",EDGE,"E69.5")}),1.0]])]});
            extrude(context, id + "F21", {"entities" : qUnion([Q0, Q1, Q2, Q3, Q4, Q5, Q6, Q7]), "endBound" : BoundingType.SYMMETRIC, "depth" : 1 * mm});
        }
        {
            var Q0;
            {var subQ0=sQuery(id+"F1.wireOp",EDGE,"E4");var subQ1=sQuery(id+"F1.wireOp",EDGE,"E2");var subQ2=makeQuery(id+"F1.imprint","INTERSECT",VERTEX,{"disambiguationData":[OD(0.0)],"derivedFrom":[subQ1,subQ0]});Q0=makeQuery(id+"F1.imprint","IMPRINT",FACE,{"disambiguationData":[TD([[makeQuery(id+"F1.imprint","IMPRINT",EDGE,{"disambiguationData":[TD([[subQ2,1.0]])],"derivedFrom":subQ1}),1.0]])]});}
            var sketch = newSketch(context, id + "F22", { "sketchPlane" : qUnion([Q0])});
            skCircle(sketch, "E71.0", {"center": v(-4.57, 31.97) * mm, "radius": 4.14 * mm});
            skArc(sketch, "E72.0", {"start": v(0.12, 30.21) * mm, "mid": v(-4.57, 36.97) * mm, "end": v(-9.25, 30.21) * mm});
            skArc(sketch, "E73.0.1", {"start": v(-0.63, 33.27) * mm, "mid": v(-4.57, 36.1) * mm, "end": v(-8.5, 33.27) * mm});
            skArc(sketch, "E73.1.0", {"start": v(-8.4, 30.41) * mm, "mid": v(-4.57, 27.82) * mm, "end": v(-0.72, 30.41) * mm});
            skArc(sketch, "E73.3.1", {"start": v(-0.72, 30.41) * mm, "mid": v(-0.42, 31.83) * mm, "end": v(-0.63, 33.27) * mm});
            skArc(sketch, "E73.3.3", {"start": v(-8.5, 33.27) * mm, "mid": v(-8.7, 31.83) * mm, "end": v(-8.4, 30.41) * mm});
            skCircle(sketch, "E74", {"center": v(-4.57, 31.97) * mm, "radius": 5 * mm});
            skLineSegment(sketch, "E75.bottom", {"start": v(3.88, 25.73) * mm, "end": v(-13.01, 25.73) * mm});
            skLineSegment(sketch, "E75.top", {"start": v(3.88, 38.2) * mm, "end": v(-13.01, 38.2) * mm});
            skLineSegment(sketch, "E75.left", {"start": v(3.88, 25.73) * mm, "end": v(3.88, 38.2) * mm});
            skLineSegment(sketch, "E75.right", {"start": v(-13.01, 25.73) * mm, "end": v(-13.01, 38.2) * mm});
            skArc(sketch, "E76.trimOffspring", {"start": v(-13.01, 28.32) * mm, "mid": v(-4.57, -5.38) * mm, "end": v(3.88, 28.32) * mm});
            skArc(sketch, "E77.trimOffspring", {"start": v(-13.01, 31.44) * mm, "mid": v(-4.57, -8.18) * mm, "end": v(3.88, 31.44) * mm});
            skLineSegment(sketch, "E78", {"start": v(-13.01, 34.42) * mm, "end": v(3.88, 34.42) * mm});
            skLineSegment(sketch, "E79", {"start": v(-13.01, 29.54) * mm, "end": v(3.88, 30.21) * mm});
            skLineSegment(sketch, "E80", {"start": v(-25.27, 12.53) * mm, "end": v(16.14, 12.53) * mm});
            skLineSegment(sketch, "E81", {"start": v(-4.57, 31.97) * mm, "end": v(-4.57, 12.53) * mm});
            skSolve(sketch);
        }
        {
            var Q0;
            {var subQ1=sQuery(id+"F22.wireOp",EDGE,"E75.top");Q0=makeQuery(id+"F22.imprint","IMPRINT",FACE,{"disambiguationData":[TD([[makeQuery(id+"F22.imprint","IMPRINT",EDGE,{"derivedFrom":subQ1}),1.0]])]});}
            var Q1;
            {var subQ5=sQuery(id+"F22.wireOp",EDGE,"E75.bottom");Q1=makeQuery(id+"F22.imprint","IMPRINT",FACE,{"disambiguationData":[TD([[makeQuery(id+"F22.imprint","IMPRINT",EDGE,{"derivedFrom":subQ5}),-1.0]])]});}
            var Q2;
            Q2=sQuery(id+"F22.wireOp",EDGE,"E80");
            revolve(context, id + "F23", {"entities" : qUnion([Q0, Q1]), "axis" : qUnion([Q2]), "revolveType" : RevolveType.FULL});
        }
        {
            var Q0;
            Q0=makeQuery(id+"F3.opRevolve","SWEPT_BODY",BODY,{"disambiguationData":[OSD([sQuery(id+"F2.wireOp",EDGE,"E45.0"),sQuery(id+"F2.wireOp",EDGE,"E46")])]});
            var Q1;
            Q1=makeQuery(id+"F5.opRevolve","SWEPT_BODY",BODY,{"disambiguationData":[OSD([sQuery(id+"F2.wireOp",EDGE,"E45.5"),sQuery(id+"F2.wireOp",EDGE,"E48")])]});
            var Q2;
            Q2=makeQuery(id+"F6.opRevolve","SWEPT_BODY",BODY,{"disambiguationData":[OSD([sQuery(id+"F2.wireOp",EDGE,"E45.4"),sQuery(id+"F2.wireOp",EDGE,"QxyX5CKa-Eoyq-XfIT-o8DO-wUQm8w5o48sP")])]});
            var Q3;
            Q3=makeQuery(id+"F6.opRevolve","SWEPT_BODY",BODY,{"disambiguationData":[OSD([sQuery(id+"F2.wireOp",EDGE,"E45.3"),sQuery(id+"F2.wireOp",EDGE,"QxyX5CKa-Eoyq-XfIT-o8DO-wUQm8w5o48sP")])]});
            var Q4;
            Q4=makeQuery(id+"F5.opRevolve","SWEPT_BODY",BODY,{"disambiguationData":[OSD([sQuery(id+"F2.wireOp",EDGE,"E45.2"),sQuery(id+"F2.wireOp",EDGE,"E48")])]});
            var Q5;
            Q5=makeQuery(id+"F3.opRevolve","SWEPT_BODY",BODY,{"disambiguationData":[OSD([sQuery(id+"F2.wireOp",EDGE,"E45.1"),sQuery(id+"F2.wireOp",EDGE,"E47")])]});
            var Q6;
            Q6=makeQuery(id+"F16.opRevolve","SWEPT_BODY",BODY,{"disambiguationData":[OSD([sQuery(id+"F8.wireOp",EDGE,"E53.1"),sQuery(id+"F8.wireOp",EDGE,"E54.0"),sQuery(id+"F8.wireOp",EDGE,"E55.0"),sQuery(id+"F8.wireOp",EDGE,"E63.trimOffspring")])]});
            var Q7;
            Q7=makeQuery(id+"F21.opExtrude","SWEPT_BODY",BODY,{"disambiguationData":[OSD([sQuery(id+"F17.wireOp",EDGE,"E69.4")])]});
            var Q8;
            Q8=sQuery(id+"F22.wireOp",EDGE,"E81");
            transform(context, id + "F24", {"entities" : qUnion([Q0, Q1, Q2, Q3, Q4, Q5, Q6, Q7]), "transformType" : TransformType.ROTATION, "transformAxis" : qUnion([Q8]), "angle" : 90 * degree, "makeCopy" : false});
        }
        {
            var Q0;
            Q0=makeQuery(id+"F23.opRevolve","SWEPT_EDGE",EDGE,{"disambiguationData":[OSD([sQuery(id+"F22.wireOp",EDGE,"E75.top"),sQuery(id+"F22.wireOp",EDGE,"E75.right")])]});
            var Q1;
            {var subQ0=sQuery(id+"F22.wireOp",EDGE,"E78");var subQ1=sQuery(id+"F22.wireOp",EDGE,"E74");Q1=makeQuery(id+"F23.opRevolve","SWEPT_EDGE",EDGE,{"disambiguationData":[OSD([subQ1,subQ0]),TDD([makeQuery(id+"F22.imprint","INTERSECT",VERTEX,{"disambiguationData":[OD(0.0)],"derivedFrom":[subQ1,subQ0]})])]});}
            var Q2;
            Q2=makeQuery(id+"F23.opRevolve","SWEPT_EDGE",EDGE,{"disambiguationData":[OSD([sQuery(id+"F22.wireOp",EDGE,"E75.right"),sQuery(id+"F22.wireOp",EDGE,"E79")])]});
            var Q3;
            Q3=makeQuery(id+"F23.opRevolve","SWEPT_EDGE",EDGE,{"disambiguationData":[OSD([sQuery(id+"F22.wireOp",EDGE,"E75.bottom"),sQuery(id+"F22.wireOp",EDGE,"E75.right")])]});
            var Q4;
            Q4=makeQuery(id+"F23.opRevolve","SWEPT_EDGE",EDGE,{"disambiguationData":[OSD([sQuery(id+"F22.wireOp",EDGE,"E75.top"),sQuery(id+"F22.wireOp",EDGE,"E75.left")])]});
            var Q5;
            Q5=makeQuery(id+"F23.opRevolve","SWEPT_EDGE",EDGE,{"disambiguationData":[OSD([sQuery(id+"F22.wireOp",EDGE,"E75.left"),sQuery(id+"F22.wireOp",EDGE,"E78")])]});
            var Q6;
            Q6=makeQuery(id+"F23.opRevolve","SWEPT_EDGE",EDGE,{"disambiguationData":[OSD([sQuery(id+"F22.wireOp",EDGE,"E75.left"),sQuery(id+"F22.wireOp",EDGE,"E79")])]});
            var Q7;
            Q7=makeQuery(id+"F23.opRevolve","SWEPT_EDGE",EDGE,{"disambiguationData":[OSD([sQuery(id+"F22.wireOp",EDGE,"E75.bottom"),sQuery(id+"F22.wireOp",EDGE,"E75.left")])]});
            fillet(context, id + "F25", {"entities" : qUnion([Q0, Q1, Q2, Q3, Q4, Q5, Q6, Q7]), "radius" : .5 * mm, "tangentPropagation" : true, "allowEdgeOverflow" : false});
        }
    });
